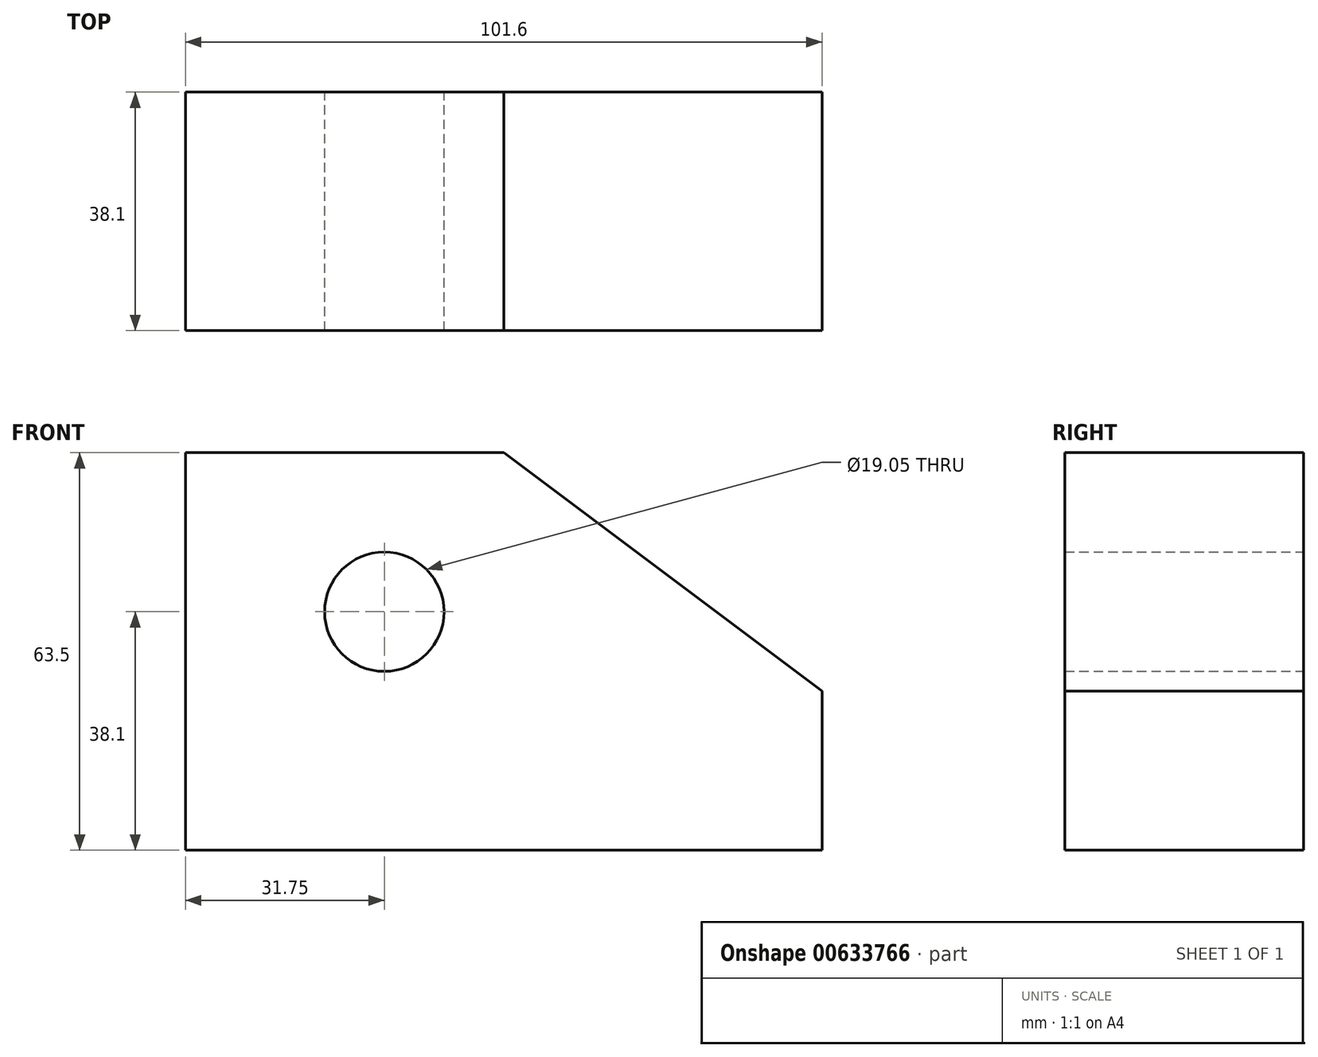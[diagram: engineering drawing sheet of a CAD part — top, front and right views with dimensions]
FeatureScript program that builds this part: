
annotation { "Feature Type Name" : "Feature", "Feature Type Description" : "" }
export const myFeature = defineFeature(function(context is Context, id is Id, definition is map)
    precondition{}
    {
        {
            var Q0;
            Q0=qCreatedBy(makeId("Front.planeOp"),FACE);
            var sketch = newSketch(context, id + "F0", { "sketchPlane" : qUnion([Q0])});
            skLineSegment(sketch, "E0", {"start": v(0, 0) * mm, "end": v(101.6, 0) * mm});
            skLineSegment(sketch, "E1", {"start": v(101.6, 0) * mm, "end": v(101.6, 25.4) * mm});
            skLineSegment(sketch, "E2", {"start": v(0, 0) * mm, "end": v(0, 63.5) * mm});
            skLineSegment(sketch, "E3", {"start": v(0, 63.5) * mm, "end": v(50.8, 63.5) * mm});
            skLineSegment(sketch, "E4", {"start": v(50.8, 63.5) * mm, "end": v(101.6, 25.4) * mm});
            skCircle(sketch, "E5", {"center": v(31.75, 38.1) * mm, "radius": 9.53 * mm});
            skSolve(sketch);
        }
        {
            var Q0;
            Q0 = qSketchRegion(id + "F0", true);
            extrude(context, id + "F1", {"entities" : qUnion([Q0]), "depth" : 38.1 * mm, "offsetDistance" : 25.4 * mm});
        }
    });
